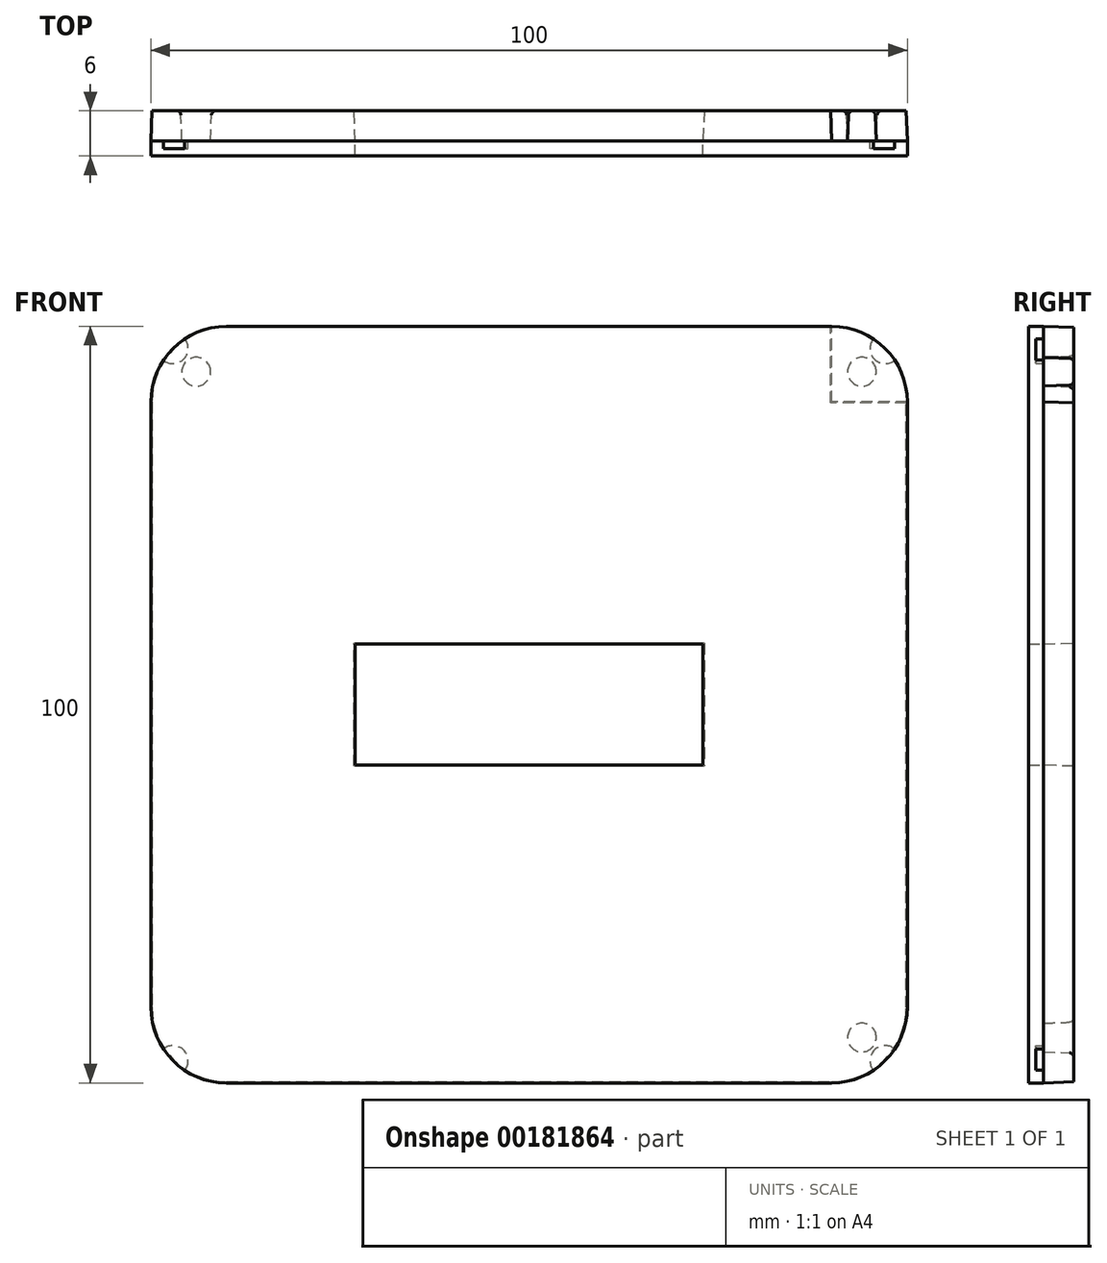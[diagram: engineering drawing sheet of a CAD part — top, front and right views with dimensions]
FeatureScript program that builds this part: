
annotation { "Feature Type Name" : "Feature", "Feature Type Description" : "" }
export const myFeature = defineFeature(function(context is Context, id is Id, definition is map)
    precondition{}
    {
        {
            var Q0;
            Q0=qCreatedBy(makeId("Front.planeOp"),FACE);
            var sketch = newSketch(context, id + "F0", { "sketchPlane" : qUnion([Q0])});
            skPoint(sketch, "E0", {"position": v(0, 50) * mm});
            skPoint(sketch, "E1", {"position": v(-50, 0) * mm});
            skLineSegment(sketch, "E2", {"start": v(40, -50) * mm, "end": v(40, -40) * mm});
            skLineSegment(sketch, "E3", {"start": v(40, -40) * mm, "end": v(50, -40) * mm});
            skArc(sketch, "E4", {"start": v(40, -50) * mm, "mid": v(47.07, -47.07) * mm, "end": v(50, -40) * mm});
            skLineSegment(sketch, "E5.MirrorCS", {"start": v(-40, -40) * mm, "end": v(-50, -40) * mm});
            skLineSegment(sketch, "E6.MirrorCS", {"start": v(-40, -50) * mm, "end": v(-40, -40) * mm});
            skArc(sketch, "E7.MirrorCS", {"start": v(-40, -50) * mm, "mid": v(-47.07, -47.07) * mm, "end": v(-50, -40) * mm});
            skLineSegment(sketch, "E8", {"start": v(-40, -50) * mm, "end": v(40, -50) * mm});
            skArc(sketch, "E9.MirrorCS", {"start": v(-40, 50) * mm, "mid": v(-47.07, 47.07) * mm, "end": v(-50, 40) * mm});
            skLineSegment(sketch, "E10.MirrorCS", {"start": v(-40, 40) * mm, "end": v(-50, 40) * mm});
            skLineSegment(sketch, "E11.MirrorCS", {"start": v(-40, 50) * mm, "end": v(-40, 40) * mm});
            skLineSegment(sketch, "E12.MirrorCS", {"start": v(-40, 50) * mm, "end": v(40, 50) * mm});
            skLineSegment(sketch, "E13.MirrorCS", {"start": v(40, 40) * mm, "end": v(50, 40) * mm});
            skLineSegment(sketch, "E14.MirrorCS", {"start": v(40, 50) * mm, "end": v(40, 40) * mm});
            skArc(sketch, "E15.MirrorCS", {"start": v(40, 50) * mm, "mid": v(47.07, 47.07) * mm, "end": v(50, 40) * mm});
            skLineSegment(sketch, "E16", {"start": v(-50, 40) * mm, "end": v(-50, -40) * mm});
            skLineSegment(sketch, "E17", {"start": v(50, 40) * mm, "end": v(50, -40) * mm});
            skLineSegment(sketch, "E18.bottom", {"start": v(-23, 8) * mm, "end": v(23, 8) * mm});
            skLineSegment(sketch, "E18.top", {"start": v(-23, -8) * mm, "end": v(23, -8) * mm});
            skLineSegment(sketch, "E18.left", {"start": v(-23, 8) * mm, "end": v(-23, -8) * mm});
            skLineSegment(sketch, "E18.right", {"start": v(23, 8) * mm, "end": v(23, -8) * mm});
            skPoint(sketch, "E19", {"position": v(0, 8) * mm});
            skPoint(sketch, "E20", {"position": v(23, 0) * mm});
            skSolve(sketch);
        }
        {
            var Q0;
            Q0 = qSketchRegion(id + "F0", true);
            extrude(context, id + "F1", {"entities" : qUnion([Q0]), "depth" : 2 * mm});
        }
        {
            var Q0;
            Q0=makeQuery(id+"F1.opExtrude","CAP_FACE",FACE,{"disambiguationData":[OSD([sQuery(id+"F0.wireOp",EDGE,"E4"),sQuery(id+"F0.wireOp",EDGE,"E7.MirrorCS"),sQuery(id+"F0.wireOp",EDGE,"E8"),sQuery(id+"F0.wireOp",EDGE,"E9.MirrorCS"),sQuery(id+"F0.wireOp",EDGE,"E12.MirrorCS"),sQuery(id+"F0.wireOp",EDGE,"E15.MirrorCS"),sQuery(id+"F0.wireOp",EDGE,"E16"),sQuery(id+"F0.wireOp",EDGE,"E17")])],"isStart":true});
            var sketch = newSketch(context, id + "F2", { "sketchPlane" : qUnion([Q0])});
            skCircle(sketch, "E21", {"center": v(-44, 44) * mm, "radius": 1.9 * mm});
            skCircle(sketch, "E22.MirrorC", {"center": v(44, 44) * mm, "radius": 1.9 * mm});
            skCircle(sketch, "E23.MirrorC", {"center": v(-44, -44) * mm, "radius": 1.9 * mm});
            skCircle(sketch, "E24.MirrorC", {"center": v(44, -44) * mm, "radius": 1.9 * mm});
            skLineSegment(sketch, "E25", {"start": v(0, 50) * mm, "end": v(-40, 50) * mm});
            skCircle(sketch, "E26.cCircle", {"center": v(0, 0) * mm, "radius": 50 * mm, "construction": true});
            skLineSegment(sketch, "E26.0", {"start": v(50, 50) * mm, "end": v(50, -50) * mm});
            skLineSegment(sketch, "E26.1", {"start": v(50, -50) * mm, "end": v(-50, -50) * mm});
            skLineSegment(sketch, "E26.2", {"start": v(-50, -50) * mm, "end": v(-50, 50) * mm});
            skLineSegment(sketch, "E26.3", {"start": v(-50, 50) * mm, "end": v(50, 50) * mm});
            skPoint(sketch, "E26.0.midPoint", {"position": v(50, 0) * mm});
            skLineSegment(sketch, "E27.bottom", {"start": v(-50, 50) * mm, "end": v(-40, 50) * mm});
            skLineSegment(sketch, "E27.top", {"start": v(-50, 40) * mm, "end": v(-40, 40) * mm});
            skLineSegment(sketch, "E27.left", {"start": v(-50, 50) * mm, "end": v(-50, 40) * mm});
            skLineSegment(sketch, "E27.right", {"start": v(-40, 50) * mm, "end": v(-40, 40) * mm});
            skSolve(sketch);
        }
        {
            var Q0;
            Q0=makeQuery(id+"F2.imprint","IMPRINT",FACE,{"disambiguationData":[TD([[makeQuery(id+"F2.imprint","IMPRINT",EDGE,{"derivedFrom":sQuery(id+"F2.wireOp",EDGE,"E21")}),1.0]])]});
            var Q1;
            Q1=makeQuery(id+"F2.imprint","IMPRINT",FACE,{"disambiguationData":[TD([[makeQuery(id+"F2.imprint","IMPRINT",EDGE,{"derivedFrom":sQuery(id+"F2.wireOp",EDGE,"E22.MirrorC")}),-1.0]])]});
            var Q2;
            Q2=makeQuery(id+"F2.imprint","IMPRINT",FACE,{"disambiguationData":[TD([[makeQuery(id+"F2.imprint","IMPRINT",EDGE,{"derivedFrom":sQuery(id+"F2.wireOp",EDGE,"E23.MirrorC")}),-1.0]])]});
            var Q3;
            Q3=makeQuery(id+"F2.imprint","IMPRINT",FACE,{"disambiguationData":[TD([[makeQuery(id+"F2.imprint","IMPRINT",EDGE,{"derivedFrom":sQuery(id+"F2.wireOp",EDGE,"E24.MirrorC")}),1.0]])]});
            extrude(context, id + "F3", {"entities" : qUnion([Q0, Q1, Q2, Q3]), "operationType" : NewBodyOperationType.ADD, "depth" : 4 * mm, "hasDraft" : true, "draftAngle" : 2 * degree, "draftPullDirection" : true});
        }
        {
            var Q0;
            Q0=makeQuery(id+"F0.imprint","IMPRINT",FACE,{"disambiguationData":[TD([[makeQuery(id+"F0.imprint","IMPRINT",EDGE,{"derivedFrom":sQuery(id+"F0.wireOp",EDGE,"E2")}),1.0]])]});
            var sketch = newSketch(context, id + "F4", { "sketchPlane" : qUnion([Q0])});
            skArc(sketch, "E28", {"start": v(45.52, 48.34) * mm, "mid": v(45.66, 45.66) * mm, "end": v(48.34, 45.52) * mm});
            skArc(sketch, "E29.MirrorCS", {"start": v(-45.52, 48.34) * mm, "mid": v(-45.66, 45.66) * mm, "end": v(-48.34, 45.52) * mm});
            skArc(sketch, "E30.MirrorCS", {"start": v(-45.52, -48.34) * mm, "mid": v(-45.66, -45.66) * mm, "end": v(-48.34, -45.52) * mm});
            skArc(sketch, "E31.MirrorCS", {"start": v(45.52, -48.34) * mm, "mid": v(45.66, -45.66) * mm, "end": v(48.34, -45.52) * mm});
            skArc(sketch, "E32", {"start": v(50, 40) * mm, "mid": v(47.07, 47.07) * mm, "end": v(40, 50) * mm});
            skLineSegment(sketch, "E33", {"start": v(40, 50) * mm, "end": v(40, 40) * mm});
            skArc(sketch, "E34.MirrorCS", {"start": v(-50, 40) * mm, "mid": v(-47.07, 47.07) * mm, "end": v(-40, 50) * mm});
            skArc(sketch, "E35.MirrorCS", {"start": v(50, -40) * mm, "mid": v(47.07, -47.07) * mm, "end": v(40, -50) * mm});
            skArc(sketch, "E36.MirrorCS", {"start": v(-50, -40) * mm, "mid": v(-47.07, -47.07) * mm, "end": v(-40, -50) * mm});
            skSolve(sketch);
        }
        {
            var Q0;
            Q0 = qSketchRegion(id + "F4", true);
            extrude(context, id + "F5", {"entities" : qUnion([Q0]), "operationType" : NewBodyOperationType.REMOVE, "depth" : 1 * mm});
        }
        {
            var Q0;
            Q0=makeQuery(id+"F3.opExtrude","CAP_EDGE",EDGE,{"disambiguationData":[OSD([sQuery(id+"FpM4sjF6zpAVGVt_1.wireOp",EDGE,"HcL5iAfH-cFwO-Oz3y-PBFi-M8xmB5XerTwz")])],"isStart":false});
            var Q1;
            Q1=makeQuery(id+"F3.opExtrude","CAP_EDGE",EDGE,{"disambiguationData":[OSD([sQuery(id+"FpM4sjF6zpAVGVt_1.wireOp",EDGE,"70866315-8b1c-4962-b7b3-250934c591660.MirrorC")])],"isStart":false});
            var Q2;
            Q2=makeQuery(id+"F3.opExtrude","CAP_EDGE",EDGE,{"disambiguationData":[OSD([sQuery(id+"FpM4sjF6zpAVGVt_1.wireOp",EDGE,"1f97ad23-a610-48cd-9a22-13fb43b591bf0.MirrorC")])],"isStart":false});
            var Q3;
            Q3=makeQuery(id+"F3.opExtrude","CAP_EDGE",EDGE,{"disambiguationData":[OSD([sQuery(id+"FpM4sjF6zpAVGVt_1.wireOp",EDGE,"2e5b538e-f65a-4f51-9bc5-026d88bbc83f0.MirrorC")])],"isStart":false});
            var Q4;
            Q4=makeQuery(id+"F3.opExtrude","CAP_EDGE",EDGE,{"disambiguationData":[OSD([sQuery(id+"F2.wireOp",EDGE,"E21")])],"isStart":false});
            var Q5;
            Q5=makeQuery(id+"F3.opExtrude","CAP_EDGE",EDGE,{"disambiguationData":[OSD([sQuery(id+"F2.wireOp",EDGE,"E23.MirrorC")])],"isStart":false});
            var Q6;
            Q6=makeQuery(id+"F3.opExtrude","CAP_EDGE",EDGE,{"disambiguationData":[OSD([sQuery(id+"F2.wireOp",EDGE,"E22.MirrorC")])],"isStart":false});
            var Q7;
            Q7=makeQuery(id+"F3.opExtrude","CAP_FACE",FACE,{"disambiguationData":[OSD([sQuery(id+"F2.wireOp",EDGE,"E24.MirrorC")])],"isStart":false});
            fillet(context, id + "F6", {"entities" : qUnion([Q0, Q1, Q2, Q3, Q4, Q5, Q6, Q7]), "radius" : 0.6 * mm, "tangentPropagation" : true, "allowEdgeOverflow" : false});
        }
    });
